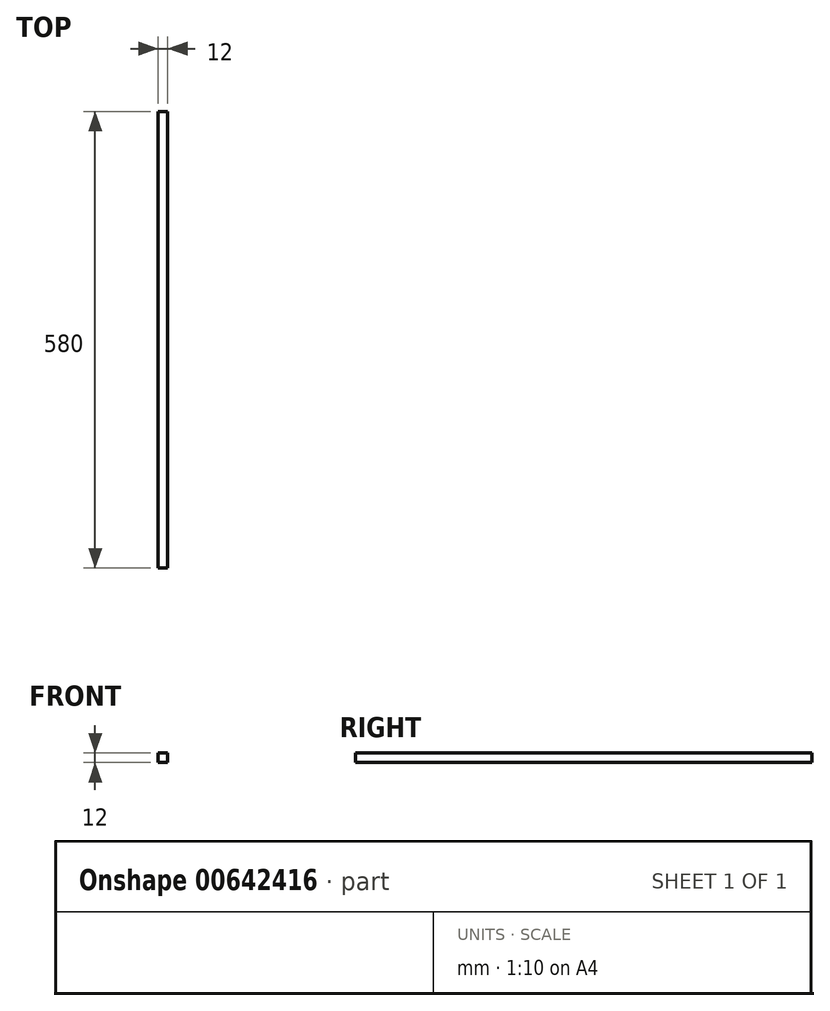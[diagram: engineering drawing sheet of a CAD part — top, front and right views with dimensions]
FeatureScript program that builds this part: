
annotation { "Feature Type Name" : "Feature", "Feature Type Description" : "" }
export const myFeature = defineFeature(function(context is Context, id is Id, definition is map)
    precondition{}
    {
        {
            var Q0;
            Q0=qCreatedBy(makeId("Front.planeOp"),FACE);
            var sketch = newSketch(context, id + "F0", { "sketchPlane" : qUnion([Q0])});
            skLineSegment(sketch, "E0.bottom", {"start": v(6, -6) * mm, "end": v(-6, -6) * mm});
            skLineSegment(sketch, "E0.top", {"start": v(6, 6) * mm, "end": v(-6, 6) * mm});
            skLineSegment(sketch, "E0.left", {"start": v(6, -6) * mm, "end": v(6, 6) * mm});
            skLineSegment(sketch, "E0.right", {"start": v(-6, -6) * mm, "end": v(-6, 6) * mm});
            skPoint(sketch, "E0.middle", {"position": v(0, 0) * mm});
            skSolve(sketch);
        }
        {
            var Q0;
            Q0=makeQuery(id+"F0.imprint","IMPRINT",FACE,{"disambiguationData":[TD([[makeQuery(id+"F0.imprint","IMPRINT",EDGE,{"derivedFrom":sQuery(id+"F0.wireOp",EDGE,"E0.bottom")}),-1.0]])]});
            extrude(context, id + "F1", {"entities" : qUnion([Q0]), "depth" : 580 * mm, "offsetDistance" : 25 * mm});
        }
    });
